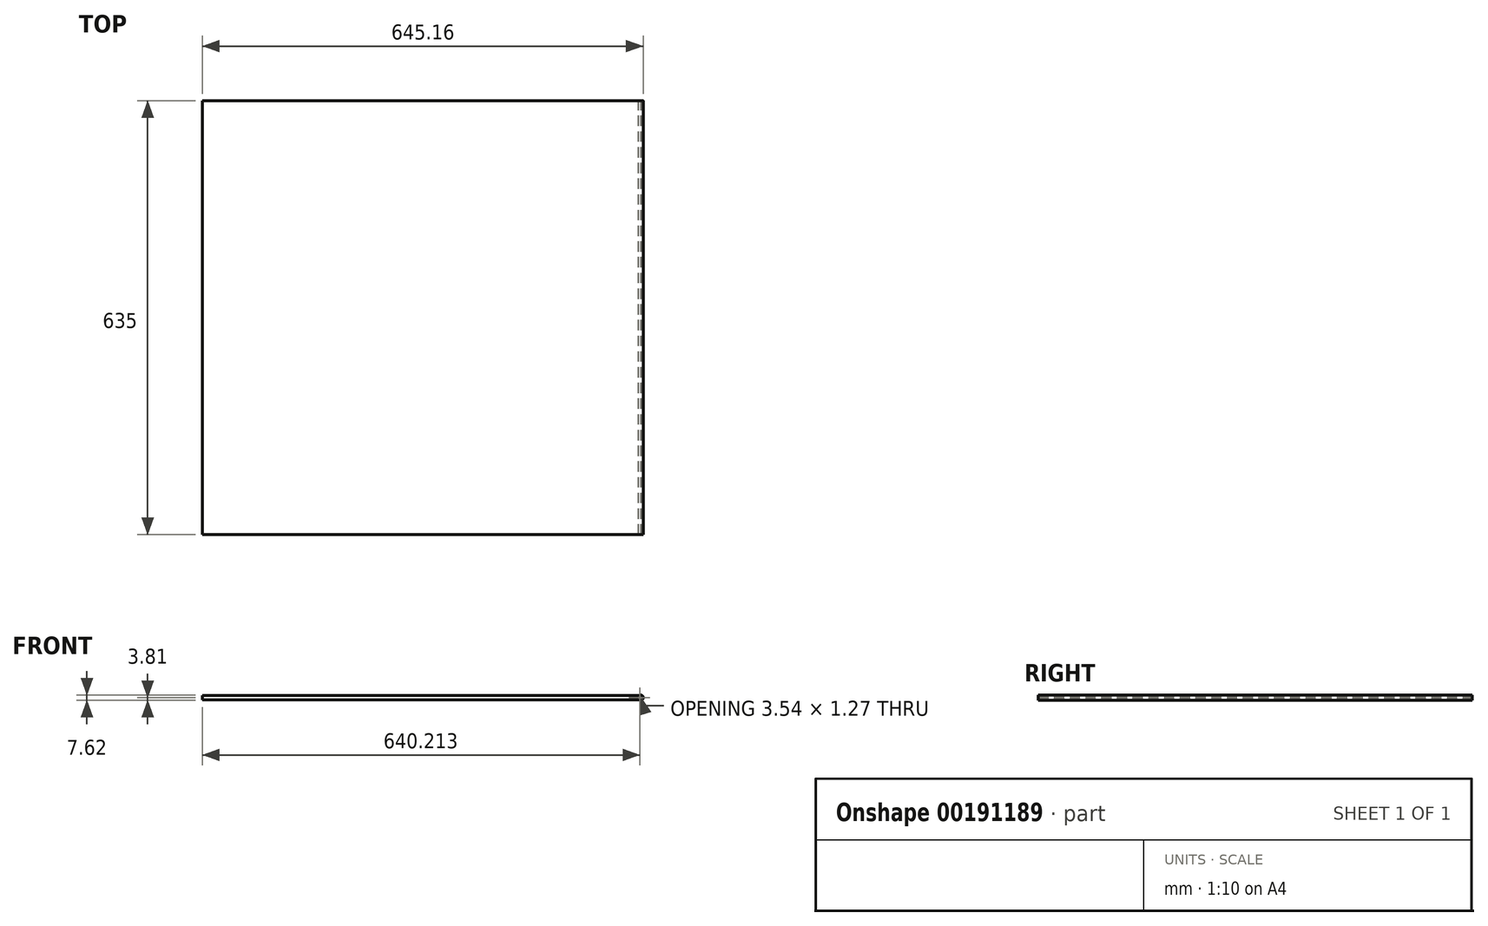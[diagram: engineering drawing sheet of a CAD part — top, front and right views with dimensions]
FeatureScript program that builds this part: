
annotation { "Feature Type Name" : "Feature", "Feature Type Description" : "" }
export const myFeature = defineFeature(function(context is Context, id is Id, definition is map)
    precondition{}
    {
        {
            var Q0;
            Q0=qCreatedBy(makeId("Front.planeOp"),FACE);
            var sketch = newSketch(context, id + "F0", { "sketchPlane" : qUnion([Q0])});
            skLineSegment(sketch, "E0.bottom", {"start": v(313.96, -3.18) * mm, "end": v(-317.5, -3.17) * mm});
            skLineSegment(sketch, "E0.top", {"start": v(313.96, 3.18) * mm, "end": v(-317.5, 3.18) * mm});
            skLineSegment(sketch, "E0.left", {"start": v(317.5, -58.87) * mm, "end": v(317.5, 51.5) * mm, "construction": true});
            skLineSegment(sketch, "E0.right", {"start": v(-317.5, -23.13) * mm, "end": v(-317.5, 26.8) * mm, "construction": true});
            skPoint(sketch, "E0.middle", {"position": v(0, 0) * mm});
            skLineSegment(sketch, "E1", {"start": v(-323.85, 0) * mm, "end": v(314.6, 0) * mm});
            skPoint(sketch, "E2.newPointB", {"position": v(317.5, 3.18) * mm});
            skArc(sketch, "E2.filletArc", {"start": v(313.96, 3.18) * mm, "mid": v(315.09, 3.28) * mm, "end": v(316.17, 3.57) * mm});
            skPoint(sketch, "E3.newPointA", {"position": v(317.5, -3.18) * mm});
            skArc(sketch, "E3.filletArc", {"start": v(316.17, -3.57) * mm, "mid": v(315.09, -3.28) * mm, "end": v(313.96, -3.18) * mm});
            skArc(sketch, "E4", {"start": v(317.24, -0.58) * mm, "mid": v(318.13, 0) * mm, "end": v(317.24, 0.58) * mm});
            skArc(sketch, "E5.filletArc", {"start": v(317.24, -0.58) * mm, "mid": v(315.94, -0.15) * mm, "end": v(314.6, 0) * mm});
            skArc(sketch, "E6.filletArc", {"start": v(314.6, 0) * mm, "mid": v(315.94, 0.15) * mm, "end": v(317.24, 0.58) * mm});
            skArc(sketch, "E7.converted", {"start": v(316.17, -3.57) * mm, "mid": v(321.3, 0) * mm, "end": v(316.17, 3.57) * mm});
            skLineSegment(sketch, "E8", {"start": v(-317.5, -3.17) * mm, "end": v(-323.85, -3.17) * mm});
            skLineSegment(sketch, "E9", {"start": v(-323.85, -3.18) * mm, "end": v(-323.85, 3.18) * mm});
            skLineSegment(sketch, "E10", {"start": v(-323.85, 3.18) * mm, "end": v(-317.5, 3.18) * mm});
            skPoint(sketch, "E11.orphan", {"position": v(-317.5, 0) * mm});
            skSolve(sketch);
        }
        {
            var Q0;
            Q0 = qSketchRegion(id + "F0", true);
            extrude(context, id + "F1", {"entities" : qUnion([Q0]), "depth" : 635 * mm});
        }
    });
